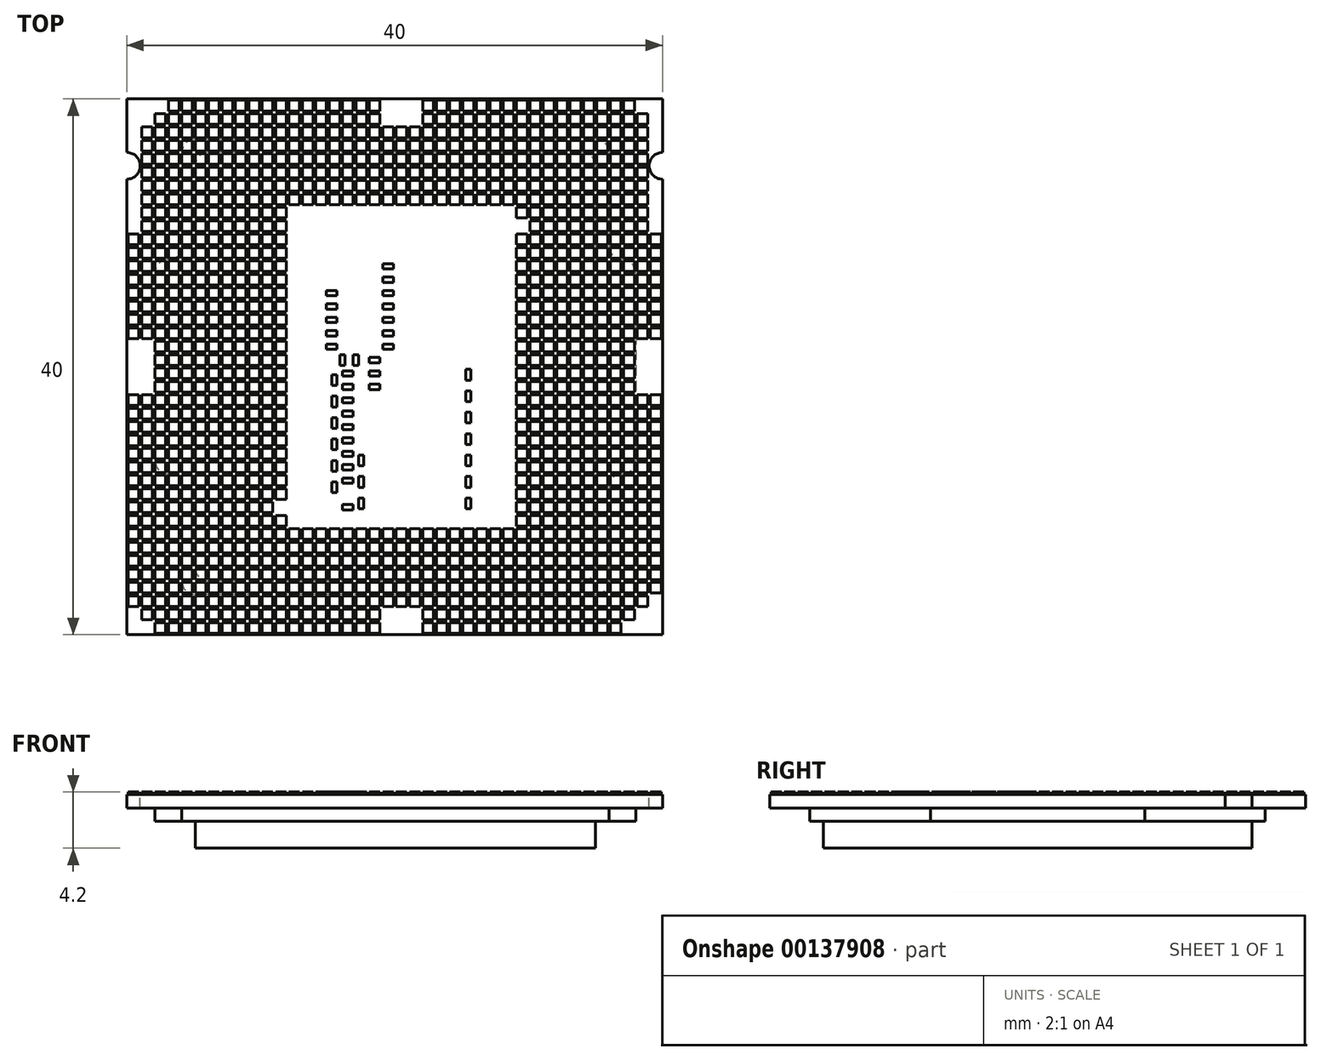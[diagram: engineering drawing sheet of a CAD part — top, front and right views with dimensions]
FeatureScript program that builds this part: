
annotation { "Feature Type Name" : "Feature", "Feature Type Description" : "" }
export const myFeature = defineFeature(function(context is Context, id is Id, definition is map)
    precondition{}
    {
        {
            var Q0;
            Q0=qCreatedBy(makeId("Top.planeOp"),FACE);
            var sketch = newSketch(context, id + "F0", { "sketchPlane" : qUnion([Q0])});
            skLineSegment(sketch, "E0.bottom", {"start": v(0, 0) * mm, "end": v(40, 0) * mm});
            skLineSegment(sketch, "E0.top", {"start": v(0, 40) * mm, "end": v(40, 40) * mm});
            skLineSegment(sketch, "E0.left", {"start": v(0, 0) * mm, "end": v(0, 40) * mm});
            skLineSegment(sketch, "E0.right", {"start": v(40, 0) * mm, "end": v(40, 40) * mm});
            skSolve(sketch);
        }
        {
            var Q0;
            Q0 = qSketchRegion(id + "F0", true);
            extrude(context, id + "F1", {"entities" : qUnion([Q0]), "oppositeDirection" : true, "depth" : 1 * mm});
        }
        {
            var Q0;
            Q0=makeQuery(id+"F1.opExtrude","CAP_FACE",FACE,{"disambiguationData":[OSD([sQuery(id+"F0.wireOp",EDGE,"E0.bottom"),sQuery(id+"F0.wireOp",EDGE,"E0.top"),sQuery(id+"F0.wireOp",EDGE,"E0.left"),sQuery(id+"F0.wireOp",EDGE,"E0.right")])],"isStart":true});
            var sketch = newSketch(context, id + "F2", { "sketchPlane" : qUnion([Q0])});
            skCircle(sketch, "E1", {"center": v(0, 35) * mm, "radius": 1 * mm});
            skCircle(sketch, "E2", {"center": v(40, 35) * mm, "radius": 1 * mm});
            skSolve(sketch);
        }
        {
            var Q0;
            Q0 = qSketchRegion(id + "F2", true);
            extrude(context, id + "F3", {"entities" : qUnion([Q0]), "operationType" : NewBodyOperationType.REMOVE, "oppositeDirection" : true, "depth" : 1 * mm});
        }
        {
            var Q0;
            Q0=makeQuery(id+"F1.opExtrude","CAP_FACE",FACE,{"disambiguationData":[OSD([sQuery(id+"F0.wireOp",EDGE,"E0.bottom"),sQuery(id+"F0.wireOp",EDGE,"E0.top"),sQuery(id+"F0.wireOp",EDGE,"E0.left"),sQuery(id+"F0.wireOp",EDGE,"E0.right")])],"isStart":true});
            var sketch = newSketch(context, id + "F4", { "sketchPlane" : qUnion([Q0])});
            skLineSegment(sketch, "E3.bottom", {"start": v(0.1, 30) * mm, "end": v(1, 30) * mm});
            skLineSegment(sketch, "E3.top", {"start": v(0.1, 22) * mm, "end": v(1, 22) * mm});
            skLineSegment(sketch, "E3.left", {"start": v(0.1, 30) * mm, "end": v(0.1, 22) * mm});
            skLineSegment(sketch, "E3.right", {"start": v(1, 30) * mm, "end": v(1, 22) * mm});
            skLineSegment(sketch, "E4.bottom", {"start": v(1, 2) * mm, "end": v(0.1, 2) * mm});
            skLineSegment(sketch, "E4.top", {"start": v(1, 18) * mm, "end": v(0.1, 18) * mm});
            skLineSegment(sketch, "E4.left", {"start": v(1, 2) * mm, "end": v(1, 18) * mm});
            skLineSegment(sketch, "E4.right", {"start": v(0.1, 2) * mm, "end": v(0.1, 18) * mm});
            skLineSegment(sketch, "E5.bottom", {"start": v(1, 22) * mm, "end": v(2, 22) * mm});
            skLineSegment(sketch, "E5.top", {"start": v(1, 38) * mm, "end": v(2, 38) * mm});
            skLineSegment(sketch, "E5.left", {"start": v(1, 22) * mm, "end": v(1, 38) * mm});
            skLineSegment(sketch, "E5.right", {"start": v(2, 22) * mm, "end": v(2, 38) * mm});
            skLineSegment(sketch, "E6.bottom", {"start": v(2, 39) * mm, "end": v(3, 39) * mm});
            skLineSegment(sketch, "E6.top", {"start": v(2, 0) * mm, "end": v(3, 0) * mm});
            skLineSegment(sketch, "E6.left", {"start": v(2, 39) * mm, "end": v(2, 0) * mm});
            skLineSegment(sketch, "E6.right", {"start": v(3, 39) * mm, "end": v(3, 0) * mm});
            skLineSegment(sketch, "E7.bottom", {"start": v(1, 18) * mm, "end": v(2, 18) * mm});
            skLineSegment(sketch, "E7.top", {"start": v(1, 1) * mm, "end": v(2, 1) * mm});
            skLineSegment(sketch, "E7.left", {"start": v(1, 18) * mm, "end": v(1, 1) * mm});
            skLineSegment(sketch, "E7.right", {"start": v(2, 18) * mm, "end": v(2, 1) * mm});
            skLineSegment(sketch, "E8.bottom", {"start": v(11, 40) * mm, "end": v(3, 40) * mm});
            skLineSegment(sketch, "E8.top", {"start": v(11, 0) * mm, "end": v(3, 0) * mm});
            skLineSegment(sketch, "E8.left", {"start": v(11, 40) * mm, "end": v(11, 0) * mm});
            skLineSegment(sketch, "E8.right", {"start": v(3, 40) * mm, "end": v(3, 0) * mm});
            skLineSegment(sketch, "E9.bottom", {"start": v(11, 40) * mm, "end": v(12, 40) * mm});
            skLineSegment(sketch, "E9.top", {"start": v(11, 10) * mm, "end": v(12, 10) * mm});
            skLineSegment(sketch, "E9.left", {"start": v(11, 40) * mm, "end": v(11, 10) * mm});
            skLineSegment(sketch, "E9.right", {"start": v(12, 40) * mm, "end": v(12, 10) * mm});
            skLineSegment(sketch, "E10.bottom", {"start": v(11, 0) * mm, "end": v(12, 0) * mm});
            skLineSegment(sketch, "E10.top", {"start": v(11, 9) * mm, "end": v(12, 9) * mm});
            skLineSegment(sketch, "E10.left", {"start": v(11, 0) * mm, "end": v(11, 9) * mm});
            skLineSegment(sketch, "E10.right", {"start": v(12, 0) * mm, "end": v(12, 9) * mm});
            skLineSegment(sketch, "E11.bottom", {"start": v(12, 40) * mm, "end": v(19, 40) * mm});
            skLineSegment(sketch, "E11.top", {"start": v(12, 32) * mm, "end": v(19, 32) * mm});
            skLineSegment(sketch, "E11.left", {"start": v(12, 40) * mm, "end": v(12, 32) * mm});
            skLineSegment(sketch, "E11.right", {"start": v(19, 40) * mm, "end": v(19, 32) * mm});
            skLineSegment(sketch, "E12.bottom", {"start": v(12, 0) * mm, "end": v(19, 0) * mm});
            skLineSegment(sketch, "E12.top", {"start": v(12, 8) * mm, "end": v(19, 8) * mm});
            skLineSegment(sketch, "E12.left", {"start": v(12, 0) * mm, "end": v(12, 8) * mm});
            skLineSegment(sketch, "E12.right", {"start": v(19, 0) * mm, "end": v(19, 8) * mm});
            skLineSegment(sketch, "E13.bottom", {"start": v(19, 8) * mm, "end": v(22, 8) * mm});
            skLineSegment(sketch, "E13.top", {"start": v(19, 2) * mm, "end": v(22, 2) * mm});
            skLineSegment(sketch, "E13.left", {"start": v(19, 8) * mm, "end": v(19, 2) * mm});
            skLineSegment(sketch, "E13.right", {"start": v(22, 8) * mm, "end": v(22, 2) * mm});
            skLineSegment(sketch, "E14.bottom", {"start": v(19, 32) * mm, "end": v(22, 32) * mm});
            skLineSegment(sketch, "E14.top", {"start": v(19, 38) * mm, "end": v(22, 38) * mm});
            skLineSegment(sketch, "E14.left", {"start": v(19, 32) * mm, "end": v(19, 38) * mm});
            skLineSegment(sketch, "E14.right", {"start": v(22, 32) * mm, "end": v(22, 38) * mm});
            skLineSegment(sketch, "E15.bottom", {"start": v(22, 32) * mm, "end": v(29, 32) * mm});
            skLineSegment(sketch, "E15.top", {"start": v(22, 40) * mm, "end": v(29, 40) * mm});
            skLineSegment(sketch, "E15.left", {"start": v(22, 32) * mm, "end": v(22, 40) * mm});
            skLineSegment(sketch, "E15.right", {"start": v(29, 32) * mm, "end": v(29, 40) * mm});
            skPoint(sketch, "E16.oppositeSnap0", {"position": v(0.1, 10) * mm});
            skLineSegment(sketch, "E17.bottom", {"start": v(22, 8) * mm, "end": v(29, 8) * mm});
            skLineSegment(sketch, "E17.top", {"start": v(22, 0) * mm, "end": v(29, 0) * mm});
            skLineSegment(sketch, "E17.left", {"start": v(22, 8) * mm, "end": v(22, 0) * mm});
            skLineSegment(sketch, "E17.right", {"start": v(29, 8) * mm, "end": v(29, 0) * mm});
            skLineSegment(sketch, "E18.bottom", {"start": v(29, 40) * mm, "end": v(30, 40) * mm});
            skLineSegment(sketch, "E18.top", {"start": v(29, 31) * mm, "end": v(30, 31) * mm});
            skLineSegment(sketch, "E18.left", {"start": v(29, 40) * mm, "end": v(29, 31) * mm});
            skLineSegment(sketch, "E18.right", {"start": v(30, 40) * mm, "end": v(30, 31) * mm});
            skLineSegment(sketch, "E19.bottom", {"start": v(29, 0) * mm, "end": v(30, 0) * mm});
            skLineSegment(sketch, "E19.top", {"start": v(29, 30) * mm, "end": v(30, 30) * mm});
            skLineSegment(sketch, "E19.left", {"start": v(29, 0) * mm, "end": v(29, 30) * mm});
            skLineSegment(sketch, "E19.right", {"start": v(30, 0) * mm, "end": v(30, 30) * mm});
            skLineSegment(sketch, "E20.bottom", {"start": v(30, 40) * mm, "end": v(37, 40) * mm});
            skLineSegment(sketch, "E20.top", {"start": v(30, 0) * mm, "end": v(37, 0) * mm});
            skLineSegment(sketch, "E20.left", {"start": v(30, 40) * mm, "end": v(30, 0) * mm});
            skLineSegment(sketch, "E20.right", {"start": v(37, 40) * mm, "end": v(37, 0) * mm});
            skLineSegment(sketch, "E21.bottom", {"start": v(37, 40) * mm, "end": v(38, 40) * mm});
            skLineSegment(sketch, "E21.top", {"start": v(37, 1) * mm, "end": v(38, 1) * mm});
            skLineSegment(sketch, "E21.left", {"start": v(37, 40) * mm, "end": v(37, 1) * mm});
            skLineSegment(sketch, "E21.right", {"start": v(38, 40) * mm, "end": v(38, 1) * mm});
            skLineSegment(sketch, "E22.bottom", {"start": v(38, 39) * mm, "end": v(39, 39) * mm});
            skLineSegment(sketch, "E22.top", {"start": v(38, 22) * mm, "end": v(39, 22) * mm});
            skLineSegment(sketch, "E22.left", {"start": v(38, 39) * mm, "end": v(38, 22) * mm});
            skLineSegment(sketch, "E22.right", {"start": v(39, 39) * mm, "end": v(39, 22) * mm});
            skLineSegment(sketch, "E23.bottom", {"start": v(38, 18) * mm, "end": v(39, 18) * mm});
            skLineSegment(sketch, "E23.top", {"start": v(38, 2) * mm, "end": v(39, 2) * mm});
            skLineSegment(sketch, "E23.left", {"start": v(38, 18) * mm, "end": v(38, 2) * mm});
            skLineSegment(sketch, "E23.right", {"start": v(39, 18) * mm, "end": v(39, 2) * mm});
            skLineSegment(sketch, "E24.bottom", {"start": v(39, 18) * mm, "end": v(39.9, 18) * mm});
            skLineSegment(sketch, "E24.top", {"start": v(39, 3) * mm, "end": v(39.9, 3) * mm});
            skLineSegment(sketch, "E24.left", {"start": v(39, 18) * mm, "end": v(39, 3) * mm});
            skLineSegment(sketch, "E24.right", {"start": v(39.9, 18) * mm, "end": v(39.9, 3) * mm});
            skLineSegment(sketch, "E25.bottom", {"start": v(39, 22) * mm, "end": v(39.9, 22) * mm});
            skLineSegment(sketch, "E25.top", {"start": v(39, 30) * mm, "end": v(39.9, 30) * mm});
            skLineSegment(sketch, "E25.left", {"start": v(39, 22) * mm, "end": v(39, 30) * mm});
            skLineSegment(sketch, "E25.right", {"start": v(39.9, 22) * mm, "end": v(39.9, 30) * mm});
            skSolve(sketch);
        }
        {
            var Q0;
            Q0 = qSketchRegion(id + "F4", true);
            extrude(context, id + "F5", {"entities" : qUnion([Q0]), "depth" : 0.2 * mm});
        }
        {
            var Q0;
            Q0=makeQuery(id+"F1.opExtrude","CAP_FACE",FACE,{"disambiguationData":[OSD([sQuery(id+"F0.wireOp",EDGE,"E0.bottom"),sQuery(id+"F0.wireOp",EDGE,"E0.top"),sQuery(id+"F0.wireOp",EDGE,"E0.left"),sQuery(id+"F0.wireOp",EDGE,"E0.right")])],"isStart":true});
            var sketch = newSketch(context, id + "F6", { "sketchPlane" : qUnion([Q0])});
            skLineSegment(sketch, "E26.bottom", {"start": v(0.9, 40) * mm, "end": v(1.1, 40) * mm});
            skLineSegment(sketch, "E26.top", {"start": v(0.9, 0) * mm, "end": v(1.1, 0) * mm});
            skLineSegment(sketch, "E26.left", {"start": v(0.9, 40) * mm, "end": v(0.9, 0) * mm});
            skLineSegment(sketch, "E26.right", {"start": v(1.1, 40) * mm, "end": v(1.1, 0) * mm});
            skLineSegment(sketch, "E27.bottom", {"start": v(1.9, 40) * mm, "end": v(2.1, 40) * mm});
            skLineSegment(sketch, "E27.top", {"start": v(1.9, 0) * mm, "end": v(2.1, 0) * mm});
            skLineSegment(sketch, "E27.left", {"start": v(1.9, 40) * mm, "end": v(1.9, 0) * mm});
            skLineSegment(sketch, "E27.right", {"start": v(2.1, 40) * mm, "end": v(2.1, 0) * mm});
            skLineSegment(sketch, "E28.bottom", {"start": v(2.9, 40) * mm, "end": v(3.1, 40) * mm});
            skLineSegment(sketch, "E28.top", {"start": v(2.9, 0) * mm, "end": v(3.1, 0) * mm});
            skLineSegment(sketch, "E28.left", {"start": v(2.9, 40) * mm, "end": v(2.9, 0) * mm});
            skLineSegment(sketch, "E28.right", {"start": v(3.1, 40) * mm, "end": v(3.1, 0) * mm});
            skLineSegment(sketch, "E29.bottom", {"start": v(3.9, 40) * mm, "end": v(4.1, 40) * mm});
            skLineSegment(sketch, "E29.top", {"start": v(3.9, 0) * mm, "end": v(4.1, 0) * mm});
            skLineSegment(sketch, "E29.left", {"start": v(3.9, 40) * mm, "end": v(3.9, 0) * mm});
            skLineSegment(sketch, "E29.right", {"start": v(4.1, 40) * mm, "end": v(4.1, 0) * mm});
            skLineSegment(sketch, "E30.bottom", {"start": v(4.9, 40) * mm, "end": v(5.1, 40) * mm});
            skLineSegment(sketch, "E30.top", {"start": v(4.9, 0) * mm, "end": v(5.1, 0) * mm});
            skLineSegment(sketch, "E30.left", {"start": v(4.9, 40) * mm, "end": v(4.9, 0) * mm});
            skLineSegment(sketch, "E30.right", {"start": v(5.1, 40) * mm, "end": v(5.1, 0) * mm});
            skLineSegment(sketch, "E31.bottom", {"start": v(5.9, 40) * mm, "end": v(6.1, 40) * mm});
            skLineSegment(sketch, "E31.top", {"start": v(5.9, 0) * mm, "end": v(6.1, 0) * mm});
            skLineSegment(sketch, "E31.left", {"start": v(5.9, 40) * mm, "end": v(5.9, 0) * mm});
            skLineSegment(sketch, "E31.right", {"start": v(6.1, 40) * mm, "end": v(6.1, 0) * mm});
            skLineSegment(sketch, "E32.bottom", {"start": v(6.9, 40) * mm, "end": v(7.1, 40) * mm});
            skLineSegment(sketch, "E32.top", {"start": v(6.9, 0) * mm, "end": v(7.1, 0) * mm});
            skLineSegment(sketch, "E32.left", {"start": v(6.9, 40) * mm, "end": v(6.9, 0) * mm});
            skLineSegment(sketch, "E32.right", {"start": v(7.1, 40) * mm, "end": v(7.1, 0) * mm});
            skLineSegment(sketch, "E33.bottom", {"start": v(7.9, 40) * mm, "end": v(8.1, 40) * mm});
            skLineSegment(sketch, "E33.top", {"start": v(7.9, 0) * mm, "end": v(8.1, 0) * mm});
            skLineSegment(sketch, "E33.left", {"start": v(7.9, 40) * mm, "end": v(7.9, 0) * mm});
            skLineSegment(sketch, "E33.right", {"start": v(8.1, 40) * mm, "end": v(8.1, 0) * mm});
            skLineSegment(sketch, "E34.bottom", {"start": v(8.9, 40) * mm, "end": v(9.1, 40) * mm});
            skLineSegment(sketch, "E34.top", {"start": v(8.9, 0) * mm, "end": v(9.1, 0) * mm});
            skLineSegment(sketch, "E34.left", {"start": v(8.9, 40) * mm, "end": v(8.9, 0) * mm});
            skLineSegment(sketch, "E34.right", {"start": v(9.1, 40) * mm, "end": v(9.1, 0) * mm});
            skLineSegment(sketch, "E35.bottom", {"start": v(9.9, 40) * mm, "end": v(10.1, 40) * mm});
            skLineSegment(sketch, "E35.top", {"start": v(9.9, 0) * mm, "end": v(10.1, 0) * mm});
            skLineSegment(sketch, "E35.left", {"start": v(9.9, 40) * mm, "end": v(9.9, 0) * mm});
            skLineSegment(sketch, "E35.right", {"start": v(10.1, 40) * mm, "end": v(10.1, 0) * mm});
            skLineSegment(sketch, "E36.bottom", {"start": v(10.9, 40) * mm, "end": v(11.1, 40) * mm});
            skLineSegment(sketch, "E36.top", {"start": v(10.9, 0) * mm, "end": v(11.1, 0) * mm});
            skLineSegment(sketch, "E36.left", {"start": v(10.9, 40) * mm, "end": v(10.9, 0) * mm});
            skLineSegment(sketch, "E36.right", {"start": v(11.1, 40) * mm, "end": v(11.1, 0) * mm});
            skLineSegment(sketch, "E37.bottom", {"start": v(11.9, 40) * mm, "end": v(12.1, 40) * mm});
            skLineSegment(sketch, "E37.top", {"start": v(11.9, 0) * mm, "end": v(12.1, 0) * mm});
            skLineSegment(sketch, "E37.left", {"start": v(11.9, 40) * mm, "end": v(11.9, 0) * mm});
            skLineSegment(sketch, "E37.right", {"start": v(12.1, 40) * mm, "end": v(12.1, 0) * mm});
            skLineSegment(sketch, "E38.bottom", {"start": v(12.9, 40) * mm, "end": v(13.1, 40) * mm});
            skLineSegment(sketch, "E38.top", {"start": v(12.9, 0) * mm, "end": v(13.1, 0) * mm});
            skLineSegment(sketch, "E38.left", {"start": v(12.9, 40) * mm, "end": v(12.9, 0) * mm});
            skLineSegment(sketch, "E38.right", {"start": v(13.1, 40) * mm, "end": v(13.1, 0) * mm});
            skLineSegment(sketch, "E39.bottom", {"start": v(13.9, 40) * mm, "end": v(14.1, 40) * mm});
            skLineSegment(sketch, "E39.top", {"start": v(13.9, 0) * mm, "end": v(14.1, 0) * mm});
            skLineSegment(sketch, "E39.left", {"start": v(13.9, 40) * mm, "end": v(13.9, 0) * mm});
            skLineSegment(sketch, "E39.right", {"start": v(14.1, 40) * mm, "end": v(14.1, 0) * mm});
            skLineSegment(sketch, "E40.bottom", {"start": v(14.9, 40) * mm, "end": v(15.1, 40) * mm});
            skLineSegment(sketch, "E40.top", {"start": v(14.9, 0) * mm, "end": v(15.1, 0) * mm});
            skLineSegment(sketch, "E40.left", {"start": v(14.9, 40) * mm, "end": v(14.9, 0) * mm});
            skLineSegment(sketch, "E40.right", {"start": v(15.1, 40) * mm, "end": v(15.1, 0) * mm});
            skLineSegment(sketch, "E41.bottom", {"start": v(15.9, 40) * mm, "end": v(16.1, 40) * mm});
            skLineSegment(sketch, "E41.top", {"start": v(15.9, 0) * mm, "end": v(16.1, 0) * mm});
            skLineSegment(sketch, "E41.left", {"start": v(15.9, 40) * mm, "end": v(15.9, 0) * mm});
            skLineSegment(sketch, "E41.right", {"start": v(16.1, 40) * mm, "end": v(16.1, 0) * mm});
            skLineSegment(sketch, "E42.bottom", {"start": v(16.9, 40) * mm, "end": v(17.1, 40) * mm});
            skLineSegment(sketch, "E42.top", {"start": v(16.9, 0) * mm, "end": v(17.1, 0) * mm});
            skLineSegment(sketch, "E42.left", {"start": v(16.9, 40) * mm, "end": v(16.9, 0) * mm});
            skLineSegment(sketch, "E42.right", {"start": v(17.1, 40) * mm, "end": v(17.1, 0) * mm});
            skLineSegment(sketch, "E43.bottom", {"start": v(17.9, 40) * mm, "end": v(18.1, 40) * mm});
            skLineSegment(sketch, "E43.top", {"start": v(17.9, 0) * mm, "end": v(18.1, 0) * mm});
            skLineSegment(sketch, "E43.left", {"start": v(17.9, 40) * mm, "end": v(17.9, 0) * mm});
            skLineSegment(sketch, "E43.right", {"start": v(18.1, 40) * mm, "end": v(18.1, 0) * mm});
            skLineSegment(sketch, "E44.bottom", {"start": v(18.9, 40) * mm, "end": v(19.1, 40) * mm});
            skLineSegment(sketch, "E44.top", {"start": v(18.9, 0) * mm, "end": v(19.1, 0) * mm});
            skLineSegment(sketch, "E44.left", {"start": v(18.9, 40) * mm, "end": v(18.9, 0) * mm});
            skLineSegment(sketch, "E44.right", {"start": v(19.1, 40) * mm, "end": v(19.1, 0) * mm});
            skLineSegment(sketch, "E45.bottom", {"start": v(19.9, 40) * mm, "end": v(20.1, 40) * mm});
            skLineSegment(sketch, "E45.top", {"start": v(19.9, 0) * mm, "end": v(20.1, 0) * mm});
            skLineSegment(sketch, "E45.left", {"start": v(19.9, 40) * mm, "end": v(19.9, 0) * mm});
            skLineSegment(sketch, "E45.right", {"start": v(20.1, 40) * mm, "end": v(20.1, 0) * mm});
            skLineSegment(sketch, "E46.bottom", {"start": v(20.9, 40) * mm, "end": v(21.1, 40) * mm});
            skLineSegment(sketch, "E46.top", {"start": v(20.9, 0) * mm, "end": v(21.1, 0) * mm});
            skLineSegment(sketch, "E46.left", {"start": v(20.9, 40) * mm, "end": v(20.9, 0) * mm});
            skLineSegment(sketch, "E46.right", {"start": v(21.1, 40) * mm, "end": v(21.1, 0) * mm});
            skLineSegment(sketch, "E47.bottom", {"start": v(21.9, 40) * mm, "end": v(22.1, 40) * mm});
            skLineSegment(sketch, "E47.top", {"start": v(21.9, 0) * mm, "end": v(22.1, 0) * mm});
            skLineSegment(sketch, "E47.left", {"start": v(21.9, 40) * mm, "end": v(21.9, 0) * mm});
            skLineSegment(sketch, "E47.right", {"start": v(22.1, 40) * mm, "end": v(22.1, 0) * mm});
            skLineSegment(sketch, "E48.bottom", {"start": v(22.9, 40) * mm, "end": v(23.1, 40) * mm});
            skLineSegment(sketch, "E48.top", {"start": v(22.9, 0) * mm, "end": v(23.1, 0) * mm});
            skLineSegment(sketch, "E48.left", {"start": v(22.9, 40) * mm, "end": v(22.9, 0) * mm});
            skLineSegment(sketch, "E48.right", {"start": v(23.1, 40) * mm, "end": v(23.1, 0) * mm});
            skLineSegment(sketch, "E49.bottom", {"start": v(23.9, 40) * mm, "end": v(24.1, 40) * mm});
            skLineSegment(sketch, "E49.top", {"start": v(23.9, 0) * mm, "end": v(24.1, 0) * mm});
            skLineSegment(sketch, "E49.left", {"start": v(23.9, 40) * mm, "end": v(23.9, 0) * mm});
            skLineSegment(sketch, "E49.right", {"start": v(24.1, 40) * mm, "end": v(24.1, 0) * mm});
            skLineSegment(sketch, "E50.bottom", {"start": v(24.9, 40) * mm, "end": v(25.1, 40) * mm});
            skLineSegment(sketch, "E50.top", {"start": v(24.9, 0) * mm, "end": v(25.1, 0) * mm});
            skLineSegment(sketch, "E50.left", {"start": v(24.9, 40) * mm, "end": v(24.9, 0) * mm});
            skLineSegment(sketch, "E50.right", {"start": v(25.1, 40) * mm, "end": v(25.1, 0) * mm});
            skLineSegment(sketch, "E51.bottom", {"start": v(25.9, 40) * mm, "end": v(26.1, 40) * mm});
            skLineSegment(sketch, "E51.top", {"start": v(25.9, 0) * mm, "end": v(26.1, 0) * mm});
            skLineSegment(sketch, "E51.left", {"start": v(25.9, 40) * mm, "end": v(25.9, 0) * mm});
            skLineSegment(sketch, "E51.right", {"start": v(26.1, 40) * mm, "end": v(26.1, 0) * mm});
            skLineSegment(sketch, "E52.bottom", {"start": v(26.9, 40) * mm, "end": v(27.1, 40) * mm});
            skLineSegment(sketch, "E52.top", {"start": v(26.9, 0) * mm, "end": v(27.1, 0) * mm});
            skLineSegment(sketch, "E52.left", {"start": v(26.9, 40) * mm, "end": v(26.9, 0) * mm});
            skLineSegment(sketch, "E52.right", {"start": v(27.1, 40) * mm, "end": v(27.1, 0) * mm});
            skLineSegment(sketch, "E53.bottom", {"start": v(27.9, 40) * mm, "end": v(28.1, 40) * mm});
            skLineSegment(sketch, "E53.top", {"start": v(27.9, 0) * mm, "end": v(28.1, 0) * mm});
            skLineSegment(sketch, "E53.left", {"start": v(27.9, 40) * mm, "end": v(27.9, 0) * mm});
            skLineSegment(sketch, "E53.right", {"start": v(28.1, 40) * mm, "end": v(28.1, 0) * mm});
            skLineSegment(sketch, "E54.bottom", {"start": v(28.9, 40) * mm, "end": v(29.1, 40) * mm});
            skLineSegment(sketch, "E54.top", {"start": v(28.9, 0) * mm, "end": v(29.1, 0) * mm});
            skLineSegment(sketch, "E54.left", {"start": v(28.9, 40) * mm, "end": v(28.9, 0) * mm});
            skLineSegment(sketch, "E54.right", {"start": v(29.1, 40) * mm, "end": v(29.1, 0) * mm});
            skLineSegment(sketch, "E55.bottom", {"start": v(29.9, 40) * mm, "end": v(30.1, 40) * mm});
            skLineSegment(sketch, "E55.top", {"start": v(29.9, 0) * mm, "end": v(30.1, 0) * mm});
            skLineSegment(sketch, "E55.left", {"start": v(29.9, 40) * mm, "end": v(29.9, 0) * mm});
            skLineSegment(sketch, "E55.right", {"start": v(30.1, 40) * mm, "end": v(30.1, 0) * mm});
            skLineSegment(sketch, "E56.bottom", {"start": v(30.9, 40) * mm, "end": v(31.1, 40) * mm});
            skLineSegment(sketch, "E56.top", {"start": v(30.9, 0) * mm, "end": v(31.1, 0) * mm});
            skLineSegment(sketch, "E56.left", {"start": v(30.9, 40) * mm, "end": v(30.9, 0) * mm});
            skLineSegment(sketch, "E56.right", {"start": v(31.1, 40) * mm, "end": v(31.1, 0) * mm});
            skLineSegment(sketch, "E57.bottom", {"start": v(31.9, 40) * mm, "end": v(32.1, 40) * mm});
            skLineSegment(sketch, "E57.top", {"start": v(31.9, 0) * mm, "end": v(32.1, 0) * mm});
            skLineSegment(sketch, "E57.left", {"start": v(31.9, 40) * mm, "end": v(31.9, 0) * mm});
            skLineSegment(sketch, "E57.right", {"start": v(32.1, 40) * mm, "end": v(32.1, 0) * mm});
            skLineSegment(sketch, "E58.bottom", {"start": v(32.9, 40) * mm, "end": v(33.1, 40) * mm});
            skLineSegment(sketch, "E58.top", {"start": v(32.9, 0) * mm, "end": v(33.1, 0) * mm});
            skLineSegment(sketch, "E58.left", {"start": v(32.9, 40) * mm, "end": v(32.9, 0) * mm});
            skLineSegment(sketch, "E58.right", {"start": v(33.1, 40) * mm, "end": v(33.1, 0) * mm});
            skLineSegment(sketch, "E59.bottom", {"start": v(33.9, 40) * mm, "end": v(34.1, 40) * mm});
            skLineSegment(sketch, "E59.top", {"start": v(33.9, 0) * mm, "end": v(34.1, 0) * mm});
            skLineSegment(sketch, "E59.left", {"start": v(33.9, 40) * mm, "end": v(33.9, 0) * mm});
            skLineSegment(sketch, "E59.right", {"start": v(34.1, 40) * mm, "end": v(34.1, 0) * mm});
            skLineSegment(sketch, "E60.bottom", {"start": v(34.9, 40) * mm, "end": v(35.1, 40) * mm});
            skLineSegment(sketch, "E60.top", {"start": v(34.9, 0) * mm, "end": v(35.1, 0) * mm});
            skLineSegment(sketch, "E60.left", {"start": v(34.9, 40) * mm, "end": v(34.9, 0) * mm});
            skLineSegment(sketch, "E60.right", {"start": v(35.1, 40) * mm, "end": v(35.1, 0) * mm});
            skLineSegment(sketch, "E61.bottom", {"start": v(35.9, 40) * mm, "end": v(36.1, 40) * mm});
            skLineSegment(sketch, "E61.top", {"start": v(35.9, 0) * mm, "end": v(36.1, 0) * mm});
            skLineSegment(sketch, "E61.left", {"start": v(35.9, 40) * mm, "end": v(35.9, 0) * mm});
            skLineSegment(sketch, "E61.right", {"start": v(36.1, 40) * mm, "end": v(36.1, 0) * mm});
            skLineSegment(sketch, "E62.bottom", {"start": v(36.9, 40) * mm, "end": v(37.1, 40) * mm});
            skLineSegment(sketch, "E62.top", {"start": v(36.9, 0) * mm, "end": v(37.1, 0) * mm});
            skLineSegment(sketch, "E62.left", {"start": v(36.9, 40) * mm, "end": v(36.9, 0) * mm});
            skLineSegment(sketch, "E62.right", {"start": v(37.1, 40) * mm, "end": v(37.1, 0) * mm});
            skLineSegment(sketch, "E63.bottom", {"start": v(37.9, 40) * mm, "end": v(38.1, 40) * mm});
            skLineSegment(sketch, "E63.top", {"start": v(37.9, 0) * mm, "end": v(38.1, 0) * mm});
            skLineSegment(sketch, "E63.left", {"start": v(37.9, 40) * mm, "end": v(37.9, 0) * mm});
            skLineSegment(sketch, "E63.right", {"start": v(38.1, 40) * mm, "end": v(38.1, 0) * mm});
            skLineSegment(sketch, "E64.bottom", {"start": v(38.9, 40) * mm, "end": v(39.1, 40) * mm});
            skLineSegment(sketch, "E64.top", {"start": v(38.9, 0) * mm, "end": v(39.1, 0) * mm});
            skLineSegment(sketch, "E64.left", {"start": v(38.9, 40) * mm, "end": v(38.9, 0) * mm});
            skLineSegment(sketch, "E64.right", {"start": v(39.1, 40) * mm, "end": v(39.1, 0) * mm});
            skSolve(sketch);
        }
        {
            var Q0;
            Q0=makeQuery(id+"F1.opExtrude","CAP_FACE",FACE,{"disambiguationData":[OSD([sQuery(id+"F0.wireOp",EDGE,"E0.bottom"),sQuery(id+"F0.wireOp",EDGE,"E0.top"),sQuery(id+"F0.wireOp",EDGE,"E0.left"),sQuery(id+"F0.wireOp",EDGE,"E0.right")])],"isStart":true});
            var sketch = newSketch(context, id + "F7", { "sketchPlane" : qUnion([Q0])});
            skLineSegment(sketch, "E65.bottom", {"start": v(40, 40) * mm, "end": v(0, 40) * mm});
            skLineSegment(sketch, "E65.top", {"start": v(40, 39.9) * mm, "end": v(0, 39.9) * mm});
            skLineSegment(sketch, "E65.left", {"start": v(40, 40) * mm, "end": v(40, 39.9) * mm});
            skLineSegment(sketch, "E65.right", {"start": v(0, 40) * mm, "end": v(0, 39.9) * mm});
            skLineSegment(sketch, "E66.bottom", {"start": v(40, 0) * mm, "end": v(0, 0) * mm});
            skLineSegment(sketch, "E66.top", {"start": v(40, 0.1) * mm, "end": v(0, 0.1) * mm});
            skLineSegment(sketch, "E66.left", {"start": v(40, 0) * mm, "end": v(40, 0.1) * mm});
            skLineSegment(sketch, "E66.right", {"start": v(0, 0) * mm, "end": v(0, 0.1) * mm});
            skLineSegment(sketch, "E67.bottom", {"start": v(40, 39.1) * mm, "end": v(0, 39.1) * mm});
            skLineSegment(sketch, "E67.top", {"start": v(40, 38.9) * mm, "end": v(0, 38.9) * mm});
            skLineSegment(sketch, "E67.left", {"start": v(40, 39.1) * mm, "end": v(40, 38.9) * mm});
            skLineSegment(sketch, "E67.right", {"start": v(0, 39.1) * mm, "end": v(0, 38.9) * mm});
            skLineSegment(sketch, "E68.bottom", {"start": v(40, 38.1) * mm, "end": v(0, 38.1) * mm});
            skLineSegment(sketch, "E68.top", {"start": v(40, 37.9) * mm, "end": v(0, 37.9) * mm});
            skLineSegment(sketch, "E68.left", {"start": v(40, 38.1) * mm, "end": v(40, 37.9) * mm});
            skLineSegment(sketch, "E68.right", {"start": v(0, 38.1) * mm, "end": v(0, 37.9) * mm});
            skLineSegment(sketch, "E69.bottom", {"start": v(40, 37.1) * mm, "end": v(0, 37.1) * mm});
            skLineSegment(sketch, "E69.top", {"start": v(40, 36.9) * mm, "end": v(0, 36.9) * mm});
            skLineSegment(sketch, "E69.left", {"start": v(40, 37.1) * mm, "end": v(40, 36.9) * mm});
            skLineSegment(sketch, "E69.right", {"start": v(0, 37.1) * mm, "end": v(0, 36.9) * mm});
            skLineSegment(sketch, "E70.bottom", {"start": v(40, 36.1) * mm, "end": v(0, 36.1) * mm});
            skLineSegment(sketch, "E70.top", {"start": v(40, 35.9) * mm, "end": v(0, 35.9) * mm});
            skLineSegment(sketch, "E70.left", {"start": v(40, 36.1) * mm, "end": v(40, 35.9) * mm});
            skLineSegment(sketch, "E70.right", {"start": v(0, 36.1) * mm, "end": v(0, 35.9) * mm});
            skLineSegment(sketch, "E71.bottom", {"start": v(40, 34.9) * mm, "end": v(0, 34.9) * mm});
            skLineSegment(sketch, "E71.top", {"start": v(40, 35.1) * mm, "end": v(0, 35.1) * mm});
            skLineSegment(sketch, "E71.left", {"start": v(40, 34.9) * mm, "end": v(40, 35.1) * mm});
            skLineSegment(sketch, "E71.right", {"start": v(0, 34.9) * mm, "end": v(0, 35.1) * mm});
            skLineSegment(sketch, "E72.bottom", {"start": v(40, 33.9) * mm, "end": v(0, 33.9) * mm});
            skLineSegment(sketch, "E72.top", {"start": v(40, 34.1) * mm, "end": v(0, 34.1) * mm});
            skLineSegment(sketch, "E72.left", {"start": v(40, 33.9) * mm, "end": v(40, 34.1) * mm});
            skLineSegment(sketch, "E72.right", {"start": v(0, 33.9) * mm, "end": v(0, 34.1) * mm});
            skLineSegment(sketch, "E73.bottom", {"start": v(40, 33.1) * mm, "end": v(0, 33.1) * mm});
            skLineSegment(sketch, "E73.top", {"start": v(40, 32.9) * mm, "end": v(0, 32.9) * mm});
            skLineSegment(sketch, "E73.left", {"start": v(40, 33.1) * mm, "end": v(40, 32.9) * mm});
            skLineSegment(sketch, "E73.right", {"start": v(0, 33.1) * mm, "end": v(0, 32.9) * mm});
            skLineSegment(sketch, "E74.bottom", {"start": v(40, 32.1) * mm, "end": v(0, 32.1) * mm});
            skLineSegment(sketch, "E74.top", {"start": v(40, 31.9) * mm, "end": v(0, 31.9) * mm});
            skLineSegment(sketch, "E74.left", {"start": v(40, 32.1) * mm, "end": v(40, 31.9) * mm});
            skLineSegment(sketch, "E74.right", {"start": v(0, 32.1) * mm, "end": v(0, 31.9) * mm});
            skLineSegment(sketch, "E75.bottom", {"start": v(40, 31.1) * mm, "end": v(0, 31.1) * mm});
            skLineSegment(sketch, "E75.top", {"start": v(40, 30.9) * mm, "end": v(0, 30.9) * mm});
            skLineSegment(sketch, "E75.left", {"start": v(40, 31.1) * mm, "end": v(40, 30.9) * mm});
            skLineSegment(sketch, "E75.right", {"start": v(0, 31.1) * mm, "end": v(0, 30.9) * mm});
            skLineSegment(sketch, "E76.bottom", {"start": v(40, 30.1) * mm, "end": v(0, 30.1) * mm});
            skLineSegment(sketch, "E76.top", {"start": v(40, 29.9) * mm, "end": v(0, 29.9) * mm});
            skLineSegment(sketch, "E76.left", {"start": v(40, 30.1) * mm, "end": v(40, 29.9) * mm});
            skLineSegment(sketch, "E76.right", {"start": v(0, 30.1) * mm, "end": v(0, 29.9) * mm});
            skLineSegment(sketch, "E77.bottom", {"start": v(40, 29.1) * mm, "end": v(0, 29.1) * mm});
            skLineSegment(sketch, "E77.top", {"start": v(40, 28.9) * mm, "end": v(0, 28.9) * mm});
            skLineSegment(sketch, "E77.left", {"start": v(40, 29.1) * mm, "end": v(40, 28.9) * mm});
            skLineSegment(sketch, "E77.right", {"start": v(0, 29.1) * mm, "end": v(0, 28.9) * mm});
            skLineSegment(sketch, "E78.bottom", {"start": v(40, 28.1) * mm, "end": v(0, 28.1) * mm});
            skLineSegment(sketch, "E78.top", {"start": v(40, 27.9) * mm, "end": v(0, 27.9) * mm});
            skLineSegment(sketch, "E78.left", {"start": v(40, 28.1) * mm, "end": v(40, 27.9) * mm});
            skLineSegment(sketch, "E78.right", {"start": v(0, 28.1) * mm, "end": v(0, 27.9) * mm});
            skLineSegment(sketch, "E79.bottom", {"start": v(40, 27.1) * mm, "end": v(0, 27.1) * mm});
            skLineSegment(sketch, "E79.top", {"start": v(40, 26.9) * mm, "end": v(0, 26.9) * mm});
            skLineSegment(sketch, "E79.left", {"start": v(40, 27.1) * mm, "end": v(40, 26.9) * mm});
            skLineSegment(sketch, "E79.right", {"start": v(0, 27.1) * mm, "end": v(0, 26.9) * mm});
            skLineSegment(sketch, "E80.bottom", {"start": v(40, 26.1) * mm, "end": v(0, 26.1) * mm});
            skLineSegment(sketch, "E80.top", {"start": v(40, 25.9) * mm, "end": v(0, 25.9) * mm});
            skLineSegment(sketch, "E80.left", {"start": v(40, 26.1) * mm, "end": v(40, 25.9) * mm});
            skLineSegment(sketch, "E80.right", {"start": v(0, 26.1) * mm, "end": v(0, 25.9) * mm});
            skLineSegment(sketch, "E81.bottom", {"start": v(40, 25.1) * mm, "end": v(0, 25.1) * mm});
            skLineSegment(sketch, "E81.top", {"start": v(40, 24.9) * mm, "end": v(0, 24.9) * mm});
            skLineSegment(sketch, "E81.left", {"start": v(40, 25.1) * mm, "end": v(40, 24.9) * mm});
            skLineSegment(sketch, "E81.right", {"start": v(0, 25.1) * mm, "end": v(0, 24.9) * mm});
            skLineSegment(sketch, "E82.bottom", {"start": v(40, 24.1) * mm, "end": v(0, 24.1) * mm});
            skLineSegment(sketch, "E82.top", {"start": v(40, 23.9) * mm, "end": v(0, 23.9) * mm});
            skLineSegment(sketch, "E82.left", {"start": v(40, 24.1) * mm, "end": v(40, 23.9) * mm});
            skLineSegment(sketch, "E82.right", {"start": v(0, 24.1) * mm, "end": v(0, 23.9) * mm});
            skLineSegment(sketch, "E83.bottom", {"start": v(40, 23.1) * mm, "end": v(0, 23.1) * mm});
            skLineSegment(sketch, "E83.top", {"start": v(40, 22.9) * mm, "end": v(0, 22.9) * mm});
            skLineSegment(sketch, "E83.left", {"start": v(40, 23.1) * mm, "end": v(40, 22.9) * mm});
            skLineSegment(sketch, "E83.right", {"start": v(0, 23.1) * mm, "end": v(0, 22.9) * mm});
            skLineSegment(sketch, "E84.bottom", {"start": v(40, 22.1) * mm, "end": v(0, 22.1) * mm});
            skLineSegment(sketch, "E84.top", {"start": v(40, 21.9) * mm, "end": v(0, 21.9) * mm});
            skLineSegment(sketch, "E84.left", {"start": v(40, 22.1) * mm, "end": v(40, 21.9) * mm});
            skLineSegment(sketch, "E84.right", {"start": v(0, 22.1) * mm, "end": v(0, 21.9) * mm});
            skLineSegment(sketch, "E85.bottom", {"start": v(40, 20.9) * mm, "end": v(0, 20.9) * mm});
            skLineSegment(sketch, "E85.top", {"start": v(40, 21.1) * mm, "end": v(0, 21.1) * mm});
            skLineSegment(sketch, "E85.left", {"start": v(40, 20.9) * mm, "end": v(40, 21.1) * mm});
            skLineSegment(sketch, "E85.right", {"start": v(0, 20.9) * mm, "end": v(0, 21.1) * mm});
            skLineSegment(sketch, "E86.bottom", {"start": v(40, 20.1) * mm, "end": v(0, 20.1) * mm});
            skLineSegment(sketch, "E86.top", {"start": v(40, 19.9) * mm, "end": v(0, 19.9) * mm});
            skLineSegment(sketch, "E86.left", {"start": v(40, 20.1) * mm, "end": v(40, 19.9) * mm});
            skLineSegment(sketch, "E86.right", {"start": v(0, 20.1) * mm, "end": v(0, 19.9) * mm});
            skLineSegment(sketch, "E87.bottom", {"start": v(40, 19.1) * mm, "end": v(0, 19.1) * mm});
            skLineSegment(sketch, "E87.top", {"start": v(40, 18.9) * mm, "end": v(0, 18.9) * mm});
            skLineSegment(sketch, "E87.left", {"start": v(40, 19.1) * mm, "end": v(40, 18.9) * mm});
            skLineSegment(sketch, "E87.right", {"start": v(0, 19.1) * mm, "end": v(0, 18.9) * mm});
            skLineSegment(sketch, "E88.bottom", {"start": v(40, 18.1) * mm, "end": v(0, 18.1) * mm});
            skLineSegment(sketch, "E88.top", {"start": v(40, 17.9) * mm, "end": v(0, 17.9) * mm});
            skLineSegment(sketch, "E88.left", {"start": v(40, 18.1) * mm, "end": v(40, 17.9) * mm});
            skLineSegment(sketch, "E88.right", {"start": v(0, 18.1) * mm, "end": v(0, 17.9) * mm});
            skLineSegment(sketch, "E89.bottom", {"start": v(40, 17.1) * mm, "end": v(0, 17.1) * mm});
            skLineSegment(sketch, "E89.top", {"start": v(40, 16.9) * mm, "end": v(0, 16.9) * mm});
            skLineSegment(sketch, "E89.left", {"start": v(40, 17.1) * mm, "end": v(40, 16.9) * mm});
            skLineSegment(sketch, "E89.right", {"start": v(0, 17.1) * mm, "end": v(0, 16.9) * mm});
            skLineSegment(sketch, "E90.bottom", {"start": v(40, 16.1) * mm, "end": v(0, 16.1) * mm});
            skLineSegment(sketch, "E90.top", {"start": v(40, 15.9) * mm, "end": v(0, 15.9) * mm});
            skLineSegment(sketch, "E90.left", {"start": v(40, 16.1) * mm, "end": v(40, 15.9) * mm});
            skLineSegment(sketch, "E90.right", {"start": v(0, 16.1) * mm, "end": v(0, 15.9) * mm});
            skLineSegment(sketch, "E91.bottom", {"start": v(40, 15.1) * mm, "end": v(0, 15.1) * mm});
            skLineSegment(sketch, "E91.top", {"start": v(40, 14.9) * mm, "end": v(0, 14.9) * mm});
            skLineSegment(sketch, "E91.left", {"start": v(40, 15.1) * mm, "end": v(40, 14.9) * mm});
            skLineSegment(sketch, "E91.right", {"start": v(0, 15.1) * mm, "end": v(0, 14.9) * mm});
            skLineSegment(sketch, "E92.bottom", {"start": v(40, 14.1) * mm, "end": v(0, 14.1) * mm});
            skLineSegment(sketch, "E92.top", {"start": v(40, 13.9) * mm, "end": v(0, 13.9) * mm});
            skLineSegment(sketch, "E92.left", {"start": v(40, 14.1) * mm, "end": v(40, 13.9) * mm});
            skLineSegment(sketch, "E92.right", {"start": v(0, 14.1) * mm, "end": v(0, 13.9) * mm});
            skLineSegment(sketch, "E93.bottom", {"start": v(40, 13.1) * mm, "end": v(0, 13.1) * mm});
            skLineSegment(sketch, "E93.top", {"start": v(40, 12.9) * mm, "end": v(0, 12.9) * mm});
            skLineSegment(sketch, "E93.left", {"start": v(40, 13.1) * mm, "end": v(40, 12.9) * mm});
            skLineSegment(sketch, "E93.right", {"start": v(0, 13.1) * mm, "end": v(0, 12.9) * mm});
            skLineSegment(sketch, "E94.bottom", {"start": v(40, 12.1) * mm, "end": v(0, 12.1) * mm});
            skLineSegment(sketch, "E94.top", {"start": v(40, 11.9) * mm, "end": v(0, 11.9) * mm});
            skLineSegment(sketch, "E94.left", {"start": v(40, 12.1) * mm, "end": v(40, 11.9) * mm});
            skLineSegment(sketch, "E94.right", {"start": v(0, 12.1) * mm, "end": v(0, 11.9) * mm});
            skLineSegment(sketch, "E95.bottom", {"start": v(40, 11.1) * mm, "end": v(0, 11.1) * mm});
            skLineSegment(sketch, "E95.top", {"start": v(40, 10.9) * mm, "end": v(0, 10.9) * mm});
            skLineSegment(sketch, "E95.left", {"start": v(40, 11.1) * mm, "end": v(40, 10.9) * mm});
            skLineSegment(sketch, "E95.right", {"start": v(0, 11.1) * mm, "end": v(0, 10.9) * mm});
            skLineSegment(sketch, "E96.bottom", {"start": v(40, 10.1) * mm, "end": v(0, 10.1) * mm});
            skLineSegment(sketch, "E96.top", {"start": v(40, 9.9) * mm, "end": v(0, 9.9) * mm});
            skLineSegment(sketch, "E96.left", {"start": v(40, 10.1) * mm, "end": v(40, 9.9) * mm});
            skLineSegment(sketch, "E96.right", {"start": v(0, 10.1) * mm, "end": v(0, 9.9) * mm});
            skLineSegment(sketch, "E97.bottom", {"start": v(40, 9.1) * mm, "end": v(0, 9.1) * mm});
            skLineSegment(sketch, "E97.top", {"start": v(40, 8.9) * mm, "end": v(0, 8.9) * mm});
            skLineSegment(sketch, "E97.left", {"start": v(40, 9.1) * mm, "end": v(40, 8.9) * mm});
            skLineSegment(sketch, "E97.right", {"start": v(0, 9.1) * mm, "end": v(0, 8.9) * mm});
            skLineSegment(sketch, "E98.bottom", {"start": v(40, 8.1) * mm, "end": v(0, 8.1) * mm});
            skLineSegment(sketch, "E98.top", {"start": v(40, 7.9) * mm, "end": v(0, 7.9) * mm});
            skLineSegment(sketch, "E98.left", {"start": v(40, 8.1) * mm, "end": v(40, 7.9) * mm});
            skLineSegment(sketch, "E98.right", {"start": v(0, 8.1) * mm, "end": v(0, 7.9) * mm});
            skLineSegment(sketch, "E99.bottom", {"start": v(40, 7.1) * mm, "end": v(0, 7.1) * mm});
            skLineSegment(sketch, "E99.top", {"start": v(40, 6.9) * mm, "end": v(0, 6.9) * mm});
            skLineSegment(sketch, "E99.left", {"start": v(40, 7.1) * mm, "end": v(40, 6.9) * mm});
            skLineSegment(sketch, "E99.right", {"start": v(0, 7.1) * mm, "end": v(0, 6.9) * mm});
            skLineSegment(sketch, "E100.bottom", {"start": v(40, 6.1) * mm, "end": v(0, 6.1) * mm});
            skLineSegment(sketch, "E100.top", {"start": v(40, 5.9) * mm, "end": v(0, 5.9) * mm});
            skLineSegment(sketch, "E100.left", {"start": v(40, 6.1) * mm, "end": v(40, 5.9) * mm});
            skLineSegment(sketch, "E100.right", {"start": v(0, 6.1) * mm, "end": v(0, 5.9) * mm});
            skLineSegment(sketch, "E101.bottom", {"start": v(40, 5.1) * mm, "end": v(0, 5.1) * mm});
            skLineSegment(sketch, "E101.top", {"start": v(40, 4.9) * mm, "end": v(0, 4.9) * mm});
            skLineSegment(sketch, "E101.left", {"start": v(40, 5.1) * mm, "end": v(40, 4.9) * mm});
            skLineSegment(sketch, "E101.right", {"start": v(0, 5.1) * mm, "end": v(0, 4.9) * mm});
            skLineSegment(sketch, "E102.bottom", {"start": v(40, 4.1) * mm, "end": v(0, 4.1) * mm});
            skLineSegment(sketch, "E102.top", {"start": v(40, 3.9) * mm, "end": v(0, 3.9) * mm});
            skLineSegment(sketch, "E102.left", {"start": v(40, 4.1) * mm, "end": v(40, 3.9) * mm});
            skLineSegment(sketch, "E102.right", {"start": v(0, 4.1) * mm, "end": v(0, 3.9) * mm});
            skLineSegment(sketch, "E103.bottom", {"start": v(40, 2.9) * mm, "end": v(0, 2.9) * mm});
            skLineSegment(sketch, "E103.top", {"start": v(40, 3.1) * mm, "end": v(0, 3.1) * mm});
            skLineSegment(sketch, "E103.left", {"start": v(40, 2.9) * mm, "end": v(40, 3.1) * mm});
            skLineSegment(sketch, "E103.right", {"start": v(0, 2.9) * mm, "end": v(0, 3.1) * mm});
            skLineSegment(sketch, "E104.bottom", {"start": v(40, 1.9) * mm, "end": v(0, 1.9) * mm});
            skLineSegment(sketch, "E104.top", {"start": v(40, 2.1) * mm, "end": v(0, 2.1) * mm});
            skLineSegment(sketch, "E104.left", {"start": v(40, 1.9) * mm, "end": v(40, 2.1) * mm});
            skLineSegment(sketch, "E104.right", {"start": v(0, 1.9) * mm, "end": v(0, 2.1) * mm});
            skLineSegment(sketch, "E105.bottom", {"start": v(40, 0.9) * mm, "end": v(0, 0.9) * mm});
            skLineSegment(sketch, "E105.top", {"start": v(40, 1.1) * mm, "end": v(0, 1.1) * mm});
            skLineSegment(sketch, "E105.left", {"start": v(40, 0.9) * mm, "end": v(40, 1.1) * mm});
            skLineSegment(sketch, "E105.right", {"start": v(0, 0.9) * mm, "end": v(0, 1.1) * mm});
            skSolve(sketch);
        }
        {
            var Q0;
            Q0 = qSketchRegion(id + "F6", true);
            extrude(context, id + "F8", {"entities" : qUnion([Q0]), "operationType" : NewBodyOperationType.REMOVE, "depth" : 1 * mm});
        }
        {
            var Q0;
            Q0 = qSketchRegion(id + "F7", true);
            extrude(context, id + "F9", {"entities" : qUnion([Q0]), "operationType" : NewBodyOperationType.REMOVE, "depth" : 1 * mm});
        }
        {
            var Q0;
            Q0=makeQuery(id+"F1.opExtrude","CAP_FACE",FACE,{"disambiguationData":[OSD([sQuery(id+"F0.wireOp",EDGE,"E0.bottom"),sQuery(id+"F0.wireOp",EDGE,"E0.top"),sQuery(id+"F0.wireOp",EDGE,"E0.left"),sQuery(id+"F0.wireOp",EDGE,"E0.right")])],"isStart":false});
            var sketch = newSketch(context, id + "F10", { "sketchPlane" : qUnion([Q0])});
            skCircle(sketch, "E106", {"center": v(35, -36) * mm, "radius": 1 * mm});
            skCircle(sketch, "E107", {"center": v(35, -4) * mm, "radius": 1 * mm});
            skLineSegment(sketch, "E108.bottom", {"start": v(35, -37) * mm, "end": v(5.1, -37) * mm});
            skLineSegment(sketch, "E108.top", {"start": v(35, -3) * mm, "end": v(5.1, -3) * mm});
            skLineSegment(sketch, "E108.left", {"start": v(35, -37) * mm, "end": v(35, -3) * mm});
            skLineSegment(sketch, "E108.right", {"start": v(5.1, -37) * mm, "end": v(5.1, -3) * mm});
            skLineSegment(sketch, "E109.bottom", {"start": v(4.1, -36) * mm, "end": v(5.1, -36) * mm});
            skLineSegment(sketch, "E109.top", {"start": v(4.1, -4) * mm, "end": v(5.1, -4) * mm});
            skLineSegment(sketch, "E109.left", {"start": v(4.1, -36) * mm, "end": v(4.1, -4) * mm});
            skLineSegment(sketch, "E109.right", {"start": v(5.1, -36) * mm, "end": v(5.1, -4) * mm});
            skLineSegment(sketch, "E110.bottom", {"start": v(36, -36) * mm, "end": v(35, -36) * mm});
            skLineSegment(sketch, "E110.top", {"start": v(36, -4) * mm, "end": v(35, -4) * mm});
            skLineSegment(sketch, "E110.left", {"start": v(36, -36) * mm, "end": v(36, -4) * mm});
            skLineSegment(sketch, "E110.right", {"start": v(35, -36) * mm, "end": v(35, -4) * mm});
            skLineSegment(sketch, "E111.bottom", {"start": v(36, -29) * mm, "end": v(37, -29) * mm});
            skLineSegment(sketch, "E111.top", {"start": v(36, -11) * mm, "end": v(37, -11) * mm});
            skLineSegment(sketch, "E111.left", {"start": v(36, -29) * mm, "end": v(36, -11) * mm});
            skLineSegment(sketch, "E111.right", {"start": v(37, -29) * mm, "end": v(37, -11) * mm});
            skLineSegment(sketch, "E112.bottom", {"start": v(4.1, -29) * mm, "end": v(3.1, -29) * mm});
            skLineSegment(sketch, "E112.top", {"start": v(4.1, -11) * mm, "end": v(3.1, -11) * mm});
            skLineSegment(sketch, "E112.left", {"start": v(4.1, -29) * mm, "end": v(4.1, -11) * mm});
            skLineSegment(sketch, "E112.right", {"start": v(3.1, -29) * mm, "end": v(3.1, -11) * mm});
            skLineSegment(sketch, "E113.bottom", {"start": v(3.1, -27) * mm, "end": v(2.1, -27) * mm});
            skLineSegment(sketch, "E113.top", {"start": v(3.1, -13) * mm, "end": v(2.1, -13) * mm});
            skLineSegment(sketch, "E113.left", {"start": v(3.1, -27) * mm, "end": v(3.1, -13) * mm});
            skLineSegment(sketch, "E113.right", {"start": v(2.1, -27) * mm, "end": v(2.1, -13) * mm});
            skLineSegment(sketch, "E114.bottom", {"start": v(37, -27) * mm, "end": v(38, -27) * mm});
            skLineSegment(sketch, "E114.top", {"start": v(37, -13) * mm, "end": v(38, -13) * mm});
            skLineSegment(sketch, "E114.left", {"start": v(37, -27) * mm, "end": v(37, -13) * mm});
            skLineSegment(sketch, "E114.right", {"start": v(38, -27) * mm, "end": v(38, -13) * mm});
            skCircle(sketch, "E115", {"center": v(5.1, -36) * mm, "radius": 1 * mm});
            skCircle(sketch, "E116", {"center": v(5.1, -4) * mm, "radius": 1 * mm});
            skSolve(sketch);
        }
        {
            var Q0;
            Q0 = qSketchRegion(id + "F10", true);
            extrude(context, id + "F11", {"entities" : qUnion([Q0]), "depth" : 1 * mm});
        }
        {
            var Q0;
            Q0=makeQuery(id+"F11.opExtrude","CAP_FACE",FACE,{"disambiguationData":[OSD([sQuery(id+"F10.wireOp",EDGE,"E106"),sQuery(id+"F10.wireOp",EDGE,"E107"),sQuery(id+"F10.wireOp",EDGE,"BgA77Dz9-5KGh-Efrp-Hv6M-BgwUDxvD4Rni"),sQuery(id+"F10.wireOp",EDGE,"gzdvfRr6-IRiG-GsUh-SExL-255vmCyJLMX6"),sQuery(id+"F10.wireOp",EDGE,"E108.bottom"),sQuery(id+"F10.wireOp",EDGE,"E108.top"),sQuery(id+"F10.wireOp",EDGE,"E108.right"),sQuery(id+"F10.wireOp",EDGE,"E109.left"),sQuery(id+"F10.wireOp",EDGE,"E110.left"),sQuery(id+"F10.wireOp",EDGE,"E111.bottom"),sQuery(id+"F10.wireOp",EDGE,"E111.top"),sQuery(id+"F10.wireOp",EDGE,"E111.right"),sQuery(id+"F10.wireOp",EDGE,"E112.bottom"),sQuery(id+"F10.wireOp",EDGE,"E112.top"),sQuery(id+"F10.wireOp",EDGE,"E112.right"),sQuery(id+"F10.wireOp",EDGE,"E113.bottom"),sQuery(id+"F10.wireOp",EDGE,"E113.top"),sQuery(id+"F10.wireOp",EDGE,"E113.right"),sQuery(id+"F10.wireOp",EDGE,"E114.bottom"),sQuery(id+"F10.wireOp",EDGE,"E114.top"),sQuery(id+"F10.wireOp",EDGE,"E114.right")])],"isStart":false});
            var sketch = newSketch(context, id + "F12", { "sketchPlane" : qUnion([Q0])});
            skCircle(sketch, "E117", {"center": v(37, -27) * mm, "radius": 1 * mm});
            skCircle(sketch, "E118", {"center": v(37, -13) * mm, "radius": 1 * mm});
            skCircle(sketch, "E119", {"center": v(3.1, -13) * mm, "radius": 1 * mm});
            skCircle(sketch, "E120", {"center": v(3.1, -27) * mm, "radius": 1 * mm});
            skSolve(sketch);
        }
        {
            var Q0;
            Q0 = qSketchRegion(id + "F12", true);
            extrude(context, id + "F13", {"entities" : qUnion([Q0]), "operationType" : NewBodyOperationType.ADD, "oppositeDirection" : true, "depth" : 1 * mm});
        }
        {
            var Q0;
            Q0=makeQuery(id+"F13.boolean.opBoolean","MERGE",FACE,{"derivedFrom":[makeQuery(id+"F11.opExtrude","CAP_FACE",FACE,{"disambiguationData":[OSD([sQuery(id+"F10.wireOp",EDGE,"E106"),sQuery(id+"F10.wireOp",EDGE,"E107"),sQuery(id+"F10.wireOp",EDGE,"BgA77Dz9-5KGh-Efrp-Hv6M-BgwUDxvD4Rni"),sQuery(id+"F10.wireOp",EDGE,"gzdvfRr6-IRiG-GsUh-SExL-255vmCyJLMX6"),sQuery(id+"F10.wireOp",EDGE,"E108.bottom"),sQuery(id+"F10.wireOp",EDGE,"E108.top"),sQuery(id+"F10.wireOp",EDGE,"E108.right"),sQuery(id+"F10.wireOp",EDGE,"E109.left"),sQuery(id+"F10.wireOp",EDGE,"E110.left"),sQuery(id+"F10.wireOp",EDGE,"E111.bottom"),sQuery(id+"F10.wireOp",EDGE,"E111.top"),sQuery(id+"F10.wireOp",EDGE,"E111.right"),sQuery(id+"F10.wireOp",EDGE,"E112.bottom"),sQuery(id+"F10.wireOp",EDGE,"E112.top"),sQuery(id+"F10.wireOp",EDGE,"E112.right"),sQuery(id+"F10.wireOp",EDGE,"E113.bottom"),sQuery(id+"F10.wireOp",EDGE,"E113.top"),sQuery(id+"F10.wireOp",EDGE,"E113.right"),sQuery(id+"F10.wireOp",EDGE,"E114.bottom"),sQuery(id+"F10.wireOp",EDGE,"E114.top"),sQuery(id+"F10.wireOp",EDGE,"E114.right")])],"isStart":false}),makeQuery(id+"F13.opExtrude","CAP_FACE",FACE,{"disambiguationData":[OSD([sQuery(id+"F12.wireOp",EDGE,"E117")])],"isStart":true}),makeQuery(id+"F13.opExtrude","CAP_FACE",FACE,{"disambiguationData":[OSD([sQuery(id+"F12.wireOp",EDGE,"E118")])],"isStart":true}),makeQuery(id+"F13.opExtrude","CAP_FACE",FACE,{"disambiguationData":[OSD([sQuery(id+"F12.wireOp",EDGE,"E119")])],"isStart":true}),makeQuery(id+"F13.opExtrude","CAP_FACE",FACE,{"disambiguationData":[OSD([sQuery(id+"F12.wireOp",EDGE,"E120")])],"isStart":true})]});
            var sketch = newSketch(context, id + "F14", { "sketchPlane" : qUnion([Q0])});
            skCircle(sketch, "E121", {"center": v(37, -29) * mm, "radius": 1 * mm});
            skCircle(sketch, "E122", {"center": v(37, -11) * mm, "radius": 1 * mm});
            skCircle(sketch, "E123", {"center": v(3.1, -29) * mm, "radius": 1 * mm});
            skCircle(sketch, "E124", {"center": v(3.1, -11) * mm, "radius": 1 * mm});
            skSolve(sketch);
        }
        {
            var Q0;
            Q0 = qSketchRegion(id + "F14", true);
            extrude(context, id + "F15", {"entities" : qUnion([Q0]), "operationType" : NewBodyOperationType.REMOVE, "oppositeDirection" : true, "depth" : 1 * mm});
        }
        {
            var Q0;
            Q0=makeQuery(id+"F13.boolean.opBoolean","MERGE",FACE,{"derivedFrom":[makeQuery(id+"F11.opExtrude","CAP_FACE",FACE,{"disambiguationData":[OSD([sQuery(id+"F10.wireOp",EDGE,"E106"),sQuery(id+"F10.wireOp",EDGE,"E107"),sQuery(id+"F10.wireOp",EDGE,"E108.bottom"),sQuery(id+"F10.wireOp",EDGE,"E108.top"),sQuery(id+"F10.wireOp",EDGE,"E109.left"),sQuery(id+"F10.wireOp",EDGE,"E110.left"),sQuery(id+"F10.wireOp",EDGE,"E111.bottom"),sQuery(id+"F10.wireOp",EDGE,"E111.top"),sQuery(id+"F10.wireOp",EDGE,"E111.right"),sQuery(id+"F10.wireOp",EDGE,"E112.bottom"),sQuery(id+"F10.wireOp",EDGE,"E112.top"),sQuery(id+"F10.wireOp",EDGE,"E112.right"),sQuery(id+"F10.wireOp",EDGE,"E113.bottom"),sQuery(id+"F10.wireOp",EDGE,"E113.top"),sQuery(id+"F10.wireOp",EDGE,"E113.right"),sQuery(id+"F10.wireOp",EDGE,"E114.bottom"),sQuery(id+"F10.wireOp",EDGE,"E114.top"),sQuery(id+"F10.wireOp",EDGE,"E114.right"),sQuery(id+"F10.wireOp",EDGE,"E115"),sQuery(id+"F10.wireOp",EDGE,"E116")])],"isStart":false}),makeQuery(id+"F13.opExtrude","CAP_FACE",FACE,{"disambiguationData":[OSD([sQuery(id+"F12.wireOp",EDGE,"E117")])],"isStart":true}),makeQuery(id+"F13.opExtrude","CAP_FACE",FACE,{"disambiguationData":[OSD([sQuery(id+"F12.wireOp",EDGE,"E118")])],"isStart":true}),makeQuery(id+"F13.opExtrude","CAP_FACE",FACE,{"disambiguationData":[OSD([sQuery(id+"F12.wireOp",EDGE,"E119")])],"isStart":true}),makeQuery(id+"F13.opExtrude","CAP_FACE",FACE,{"disambiguationData":[OSD([sQuery(id+"F12.wireOp",EDGE,"E120")])],"isStart":true})]});
            var sketch = newSketch(context, id + "F16", { "sketchPlane" : qUnion([Q0])});
            skLineSegment(sketch, "E125.bottom", {"start": v(34, -36) * mm, "end": v(6.1, -36) * mm});
            skLineSegment(sketch, "E125.top", {"start": v(34, -4) * mm, "end": v(6.1, -4) * mm});
            skLineSegment(sketch, "E125.left", {"start": v(34, -36) * mm, "end": v(34, -4) * mm});
            skLineSegment(sketch, "E125.right", {"start": v(6.1, -36) * mm, "end": v(6.1, -4) * mm});
            skLineSegment(sketch, "E126.bottom", {"start": v(34, -35) * mm, "end": v(35, -35) * mm});
            skLineSegment(sketch, "E126.top", {"start": v(34, -5) * mm, "end": v(35, -5) * mm});
            skLineSegment(sketch, "E126.left", {"start": v(34, -35) * mm, "end": v(34, -5) * mm});
            skLineSegment(sketch, "E126.right", {"start": v(35, -35) * mm, "end": v(35, -5) * mm});
            skLineSegment(sketch, "E127.bottom", {"start": v(6.1, -35) * mm, "end": v(5.1, -35) * mm});
            skLineSegment(sketch, "E127.top", {"start": v(6.1, -5) * mm, "end": v(5.1, -5) * mm});
            skLineSegment(sketch, "E127.left", {"start": v(6.1, -35) * mm, "end": v(6.1, -5) * mm});
            skLineSegment(sketch, "E127.right", {"start": v(5.1, -35) * mm, "end": v(5.1, -5) * mm});
            skCircle(sketch, "E128", {"center": v(34, -35) * mm, "radius": 1 * mm});
            skCircle(sketch, "E129", {"center": v(6.1, -35) * mm, "radius": 1 * mm});
            skCircle(sketch, "E130", {"center": v(6.1, -5) * mm, "radius": 1 * mm});
            skCircle(sketch, "E131", {"center": v(34, -5) * mm, "radius": 1 * mm});
            skSolve(sketch);
        }
        {
            var Q0;
            Q0 = qSketchRegion(id + "F16", true);
            extrude(context, id + "F17", {"entities" : qUnion([Q0]), "operationType" : NewBodyOperationType.ADD, "depth" : 2 * mm});
        }
        {
            var Q0;
            Q0=makeQuery(id+"F1.opExtrude","CAP_FACE",FACE,{"disambiguationData":[OSD([sQuery(id+"F0.wireOp",EDGE,"E0.bottom"),sQuery(id+"F0.wireOp",EDGE,"E0.top"),sQuery(id+"F0.wireOp",EDGE,"E0.left"),sQuery(id+"F0.wireOp",EDGE,"E0.right")])],"isStart":true});
            var sketch = newSketch(context, id + "F18", { "sketchPlane" : qUnion([Q0])});
            skLineSegment(sketch, "E132.bottom", {"start": v(19.1, 27.7) * mm, "end": v(19.9, 27.7) * mm});
            skLineSegment(sketch, "E132.top", {"start": v(19.1, 27.3) * mm, "end": v(19.9, 27.3) * mm});
            skLineSegment(sketch, "E132.left", {"start": v(19.1, 27.7) * mm, "end": v(19.1, 27.3) * mm});
            skLineSegment(sketch, "E132.right", {"start": v(19.9, 27.7) * mm, "end": v(19.9, 27.3) * mm});
            skLineSegment(sketch, "E133.bottom", {"start": v(19.1, 26.7) * mm, "end": v(19.9, 26.7) * mm});
            skLineSegment(sketch, "E133.top", {"start": v(19.1, 26.3) * mm, "end": v(19.9, 26.3) * mm});
            skLineSegment(sketch, "E133.left", {"start": v(19.1, 26.7) * mm, "end": v(19.1, 26.3) * mm});
            skLineSegment(sketch, "E133.right", {"start": v(19.9, 26.7) * mm, "end": v(19.9, 26.3) * mm});
            skLineSegment(sketch, "E134.bottom", {"start": v(19.1, 25.7) * mm, "end": v(19.9, 25.7) * mm});
            skLineSegment(sketch, "E134.top", {"start": v(19.1, 25.3) * mm, "end": v(19.9, 25.3) * mm});
            skLineSegment(sketch, "E134.left", {"start": v(19.1, 25.7) * mm, "end": v(19.1, 25.3) * mm});
            skLineSegment(sketch, "E134.right", {"start": v(19.9, 25.7) * mm, "end": v(19.9, 25.3) * mm});
            skLineSegment(sketch, "E135.bottom", {"start": v(19.1, 24.7) * mm, "end": v(19.9, 24.7) * mm});
            skLineSegment(sketch, "E135.top", {"start": v(19.1, 24.3) * mm, "end": v(19.9, 24.3) * mm});
            skLineSegment(sketch, "E135.left", {"start": v(19.1, 24.7) * mm, "end": v(19.1, 24.3) * mm});
            skLineSegment(sketch, "E135.right", {"start": v(19.9, 24.7) * mm, "end": v(19.9, 24.3) * mm});
            skLineSegment(sketch, "E136.bottom", {"start": v(19.1, 23.7) * mm, "end": v(19.9, 23.7) * mm});
            skLineSegment(sketch, "E136.top", {"start": v(19.1, 23.3) * mm, "end": v(19.9, 23.3) * mm});
            skLineSegment(sketch, "E136.left", {"start": v(19.1, 23.7) * mm, "end": v(19.1, 23.3) * mm});
            skLineSegment(sketch, "E136.right", {"start": v(19.9, 23.7) * mm, "end": v(19.9, 23.3) * mm});
            skLineSegment(sketch, "E137.bottom", {"start": v(19.1, 22.7) * mm, "end": v(19.9, 22.7) * mm});
            skLineSegment(sketch, "E137.top", {"start": v(19.1, 22.3) * mm, "end": v(19.9, 22.3) * mm});
            skLineSegment(sketch, "E137.left", {"start": v(19.1, 22.7) * mm, "end": v(19.1, 22.3) * mm});
            skLineSegment(sketch, "E137.right", {"start": v(19.9, 22.7) * mm, "end": v(19.9, 22.3) * mm});
            skLineSegment(sketch, "E138.bottom", {"start": v(19.1, 21.7) * mm, "end": v(19.9, 21.7) * mm});
            skLineSegment(sketch, "E138.top", {"start": v(19.1, 21.3) * mm, "end": v(19.9, 21.3) * mm});
            skLineSegment(sketch, "E138.left", {"start": v(19.1, 21.7) * mm, "end": v(19.1, 21.3) * mm});
            skLineSegment(sketch, "E138.right", {"start": v(19.9, 21.7) * mm, "end": v(19.9, 21.3) * mm});
            skLineSegment(sketch, "E139.bottom", {"start": v(14.9, 21.3) * mm, "end": v(15.7, 21.3) * mm});
            skLineSegment(sketch, "E139.top", {"start": v(14.9, 21.7) * mm, "end": v(15.7, 21.7) * mm});
            skLineSegment(sketch, "E139.left", {"start": v(14.9, 21.3) * mm, "end": v(14.9, 21.7) * mm});
            skLineSegment(sketch, "E139.right", {"start": v(15.7, 21.3) * mm, "end": v(15.7, 21.7) * mm});
            skLineSegment(sketch, "E140.bottom", {"start": v(14.9, 22.3) * mm, "end": v(15.7, 22.3) * mm});
            skLineSegment(sketch, "E140.top", {"start": v(14.9, 22.7) * mm, "end": v(15.7, 22.7) * mm});
            skLineSegment(sketch, "E140.left", {"start": v(14.9, 22.3) * mm, "end": v(14.9, 22.7) * mm});
            skLineSegment(sketch, "E140.right", {"start": v(15.7, 22.3) * mm, "end": v(15.7, 22.7) * mm});
            skLineSegment(sketch, "E141.bottom", {"start": v(14.9, 23.3) * mm, "end": v(15.7, 23.3) * mm});
            skLineSegment(sketch, "E141.top", {"start": v(14.9, 23.7) * mm, "end": v(15.7, 23.7) * mm});
            skLineSegment(sketch, "E141.left", {"start": v(14.9, 23.3) * mm, "end": v(14.9, 23.7) * mm});
            skLineSegment(sketch, "E141.right", {"start": v(15.7, 23.3) * mm, "end": v(15.7, 23.7) * mm});
            skLineSegment(sketch, "E142.bottom", {"start": v(15.7, 24.3) * mm, "end": v(14.9, 24.3) * mm});
            skLineSegment(sketch, "E142.top", {"start": v(15.7, 24.7) * mm, "end": v(14.9, 24.7) * mm});
            skLineSegment(sketch, "E142.left", {"start": v(15.7, 24.3) * mm, "end": v(15.7, 24.7) * mm});
            skLineSegment(sketch, "E142.right", {"start": v(14.9, 24.3) * mm, "end": v(14.9, 24.7) * mm});
            skLineSegment(sketch, "E143.bottom", {"start": v(15.7, 25.3) * mm, "end": v(14.9, 25.3) * mm});
            skLineSegment(sketch, "E143.top", {"start": v(15.7, 25.7) * mm, "end": v(14.9, 25.7) * mm});
            skLineSegment(sketch, "E143.left", {"start": v(15.7, 25.3) * mm, "end": v(15.7, 25.7) * mm});
            skLineSegment(sketch, "E143.right", {"start": v(14.9, 25.3) * mm, "end": v(14.9, 25.7) * mm});
            skLineSegment(sketch, "E144.bottom", {"start": v(18.9, 20.7) * mm, "end": v(18.1, 20.7) * mm});
            skLineSegment(sketch, "E144.top", {"start": v(18.9, 20.3) * mm, "end": v(18.1, 20.3) * mm});
            skLineSegment(sketch, "E144.left", {"start": v(18.9, 20.7) * mm, "end": v(18.9, 20.3) * mm});
            skLineSegment(sketch, "E144.right", {"start": v(18.1, 20.7) * mm, "end": v(18.1, 20.3) * mm});
            skLineSegment(sketch, "E145.bottom", {"start": v(18.9, 19.7) * mm, "end": v(18.1, 19.7) * mm});
            skLineSegment(sketch, "E145.top", {"start": v(18.9, 19.3) * mm, "end": v(18.1, 19.3) * mm});
            skLineSegment(sketch, "E145.left", {"start": v(18.9, 19.7) * mm, "end": v(18.9, 19.3) * mm});
            skLineSegment(sketch, "E145.right", {"start": v(18.1, 19.7) * mm, "end": v(18.1, 19.3) * mm});
            skLineSegment(sketch, "E146.bottom", {"start": v(18.9, 18.7) * mm, "end": v(18.1, 18.7) * mm});
            skLineSegment(sketch, "E146.top", {"start": v(18.9, 18.3) * mm, "end": v(18.1, 18.3) * mm});
            skLineSegment(sketch, "E146.left", {"start": v(18.9, 18.7) * mm, "end": v(18.9, 18.3) * mm});
            skLineSegment(sketch, "E146.right", {"start": v(18.1, 18.7) * mm, "end": v(18.1, 18.3) * mm});
            skLineSegment(sketch, "E147.bottom", {"start": v(15.9, 20.9) * mm, "end": v(16.3, 20.9) * mm});
            skLineSegment(sketch, "E147.top", {"start": v(15.9, 20.1) * mm, "end": v(16.3, 20.1) * mm});
            skLineSegment(sketch, "E147.left", {"start": v(15.9, 20.9) * mm, "end": v(15.9, 20.1) * mm});
            skLineSegment(sketch, "E147.right", {"start": v(16.3, 20.9) * mm, "end": v(16.3, 20.1) * mm});
            skLineSegment(sketch, "E148.bottom", {"start": v(16.9, 20.9) * mm, "end": v(17.3, 20.9) * mm});
            skLineSegment(sketch, "E148.top", {"start": v(16.9, 20.1) * mm, "end": v(17.3, 20.1) * mm});
            skLineSegment(sketch, "E148.left", {"start": v(16.9, 20.9) * mm, "end": v(16.9, 20.1) * mm});
            skLineSegment(sketch, "E148.right", {"start": v(17.3, 20.9) * mm, "end": v(17.3, 20.1) * mm});
            skLineSegment(sketch, "E149.bottom", {"start": v(16.9, 19.7) * mm, "end": v(16.1, 19.7) * mm});
            skLineSegment(sketch, "E149.top", {"start": v(16.9, 19.3) * mm, "end": v(16.1, 19.3) * mm});
            skLineSegment(sketch, "E149.left", {"start": v(16.9, 19.7) * mm, "end": v(16.9, 19.3) * mm});
            skLineSegment(sketch, "E149.right", {"start": v(16.1, 19.7) * mm, "end": v(16.1, 19.3) * mm});
            skLineSegment(sketch, "E150.bottom", {"start": v(16.9, 18.7) * mm, "end": v(16.1, 18.7) * mm});
            skLineSegment(sketch, "E150.top", {"start": v(16.9, 18.3) * mm, "end": v(16.1, 18.3) * mm});
            skLineSegment(sketch, "E150.left", {"start": v(16.9, 18.7) * mm, "end": v(16.9, 18.3) * mm});
            skLineSegment(sketch, "E150.right", {"start": v(16.1, 18.7) * mm, "end": v(16.1, 18.3) * mm});
            skLineSegment(sketch, "E151.bottom", {"start": v(16.9, 17.7) * mm, "end": v(16.1, 17.7) * mm});
            skLineSegment(sketch, "E151.top", {"start": v(16.9, 17.3) * mm, "end": v(16.1, 17.3) * mm});
            skLineSegment(sketch, "E151.left", {"start": v(16.9, 17.7) * mm, "end": v(16.9, 17.3) * mm});
            skLineSegment(sketch, "E151.right", {"start": v(16.1, 17.7) * mm, "end": v(16.1, 17.3) * mm});
            skLineSegment(sketch, "E152.bottom", {"start": v(16.9, 16.7) * mm, "end": v(16.1, 16.7) * mm});
            skLineSegment(sketch, "E152.top", {"start": v(16.9, 16.3) * mm, "end": v(16.1, 16.3) * mm});
            skLineSegment(sketch, "E152.left", {"start": v(16.9, 16.7) * mm, "end": v(16.9, 16.3) * mm});
            skLineSegment(sketch, "E152.right", {"start": v(16.1, 16.7) * mm, "end": v(16.1, 16.3) * mm});
            skLineSegment(sketch, "E153.bottom", {"start": v(16.1, 15.7) * mm, "end": v(16.9, 15.7) * mm});
            skLineSegment(sketch, "E153.top", {"start": v(16.1, 15.3) * mm, "end": v(16.9, 15.3) * mm});
            skLineSegment(sketch, "E153.left", {"start": v(16.1, 15.7) * mm, "end": v(16.1, 15.3) * mm});
            skLineSegment(sketch, "E153.right", {"start": v(16.9, 15.7) * mm, "end": v(16.9, 15.3) * mm});
            skLineSegment(sketch, "E154.bottom", {"start": v(16.9, 14.7) * mm, "end": v(16.1, 14.7) * mm});
            skLineSegment(sketch, "E154.top", {"start": v(16.9, 14.3) * mm, "end": v(16.1, 14.3) * mm});
            skLineSegment(sketch, "E154.left", {"start": v(16.9, 14.7) * mm, "end": v(16.9, 14.3) * mm});
            skLineSegment(sketch, "E154.right", {"start": v(16.1, 14.7) * mm, "end": v(16.1, 14.3) * mm});
            skLineSegment(sketch, "E155.bottom", {"start": v(16.1, 13.7) * mm, "end": v(16.9, 13.7) * mm});
            skLineSegment(sketch, "E155.top", {"start": v(16.1, 13.3) * mm, "end": v(16.9, 13.3) * mm});
            skLineSegment(sketch, "E155.left", {"start": v(16.1, 13.7) * mm, "end": v(16.1, 13.3) * mm});
            skLineSegment(sketch, "E155.right", {"start": v(16.9, 13.7) * mm, "end": v(16.9, 13.3) * mm});
            skLineSegment(sketch, "E156.bottom", {"start": v(16.9, 12.7) * mm, "end": v(16.1, 12.7) * mm});
            skLineSegment(sketch, "E156.top", {"start": v(16.9, 12.3) * mm, "end": v(16.1, 12.3) * mm});
            skLineSegment(sketch, "E156.left", {"start": v(16.9, 12.7) * mm, "end": v(16.9, 12.3) * mm});
            skLineSegment(sketch, "E156.right", {"start": v(16.1, 12.7) * mm, "end": v(16.1, 12.3) * mm});
            skLineSegment(sketch, "E157.bottom", {"start": v(16.1, 11.7) * mm, "end": v(16.9, 11.7) * mm});
            skLineSegment(sketch, "E157.top", {"start": v(16.1, 11.3) * mm, "end": v(16.9, 11.3) * mm});
            skLineSegment(sketch, "E157.left", {"start": v(16.1, 11.7) * mm, "end": v(16.1, 11.3) * mm});
            skLineSegment(sketch, "E157.right", {"start": v(16.9, 11.7) * mm, "end": v(16.9, 11.3) * mm});
            skLineSegment(sketch, "E158.bottom", {"start": v(16.1, 9.7) * mm, "end": v(16.9, 9.7) * mm});
            skLineSegment(sketch, "E158.top", {"start": v(16.1, 9.3) * mm, "end": v(16.9, 9.3) * mm});
            skLineSegment(sketch, "E158.left", {"start": v(16.1, 9.7) * mm, "end": v(16.1, 9.3) * mm});
            skLineSegment(sketch, "E158.right", {"start": v(16.9, 9.7) * mm, "end": v(16.9, 9.3) * mm});
            skLineSegment(sketch, "E159.bottom", {"start": v(17.3, 9.4) * mm, "end": v(17.7, 9.4) * mm});
            skLineSegment(sketch, "E159.top", {"start": v(17.3, 10.2) * mm, "end": v(17.7, 10.2) * mm});
            skLineSegment(sketch, "E159.left", {"start": v(17.3, 9.4) * mm, "end": v(17.3, 10.2) * mm});
            skLineSegment(sketch, "E159.right", {"start": v(17.7, 9.4) * mm, "end": v(17.7, 10.2) * mm});
            skLineSegment(sketch, "E160.bottom", {"start": v(17.7, 11.8) * mm, "end": v(17.3, 11.8) * mm});
            skLineSegment(sketch, "E160.top", {"start": v(17.7, 11) * mm, "end": v(17.3, 11) * mm});
            skLineSegment(sketch, "E160.left", {"start": v(17.7, 11.8) * mm, "end": v(17.7, 11) * mm});
            skLineSegment(sketch, "E160.right", {"start": v(17.3, 11.8) * mm, "end": v(17.3, 11) * mm});
            skLineSegment(sketch, "E161.bottom", {"start": v(17.7, 13.4) * mm, "end": v(17.3, 13.4) * mm});
            skLineSegment(sketch, "E161.top", {"start": v(17.7, 12.6) * mm, "end": v(17.3, 12.6) * mm});
            skLineSegment(sketch, "E161.left", {"start": v(17.7, 13.4) * mm, "end": v(17.7, 12.6) * mm});
            skLineSegment(sketch, "E161.right", {"start": v(17.3, 13.4) * mm, "end": v(17.3, 12.6) * mm});
            skLineSegment(sketch, "E162.bottom", {"start": v(15.3, 19.4) * mm, "end": v(15.7, 19.4) * mm});
            skLineSegment(sketch, "E162.top", {"start": v(15.3, 18.6) * mm, "end": v(15.7, 18.6) * mm});
            skLineSegment(sketch, "E162.left", {"start": v(15.3, 19.4) * mm, "end": v(15.3, 18.6) * mm});
            skLineSegment(sketch, "E162.right", {"start": v(15.7, 19.4) * mm, "end": v(15.7, 18.6) * mm});
            skLineSegment(sketch, "E163.bottom", {"start": v(15.3, 17.8) * mm, "end": v(15.7, 17.8) * mm});
            skLineSegment(sketch, "E163.top", {"start": v(15.3, 17) * mm, "end": v(15.7, 17) * mm});
            skLineSegment(sketch, "E163.left", {"start": v(15.3, 17.8) * mm, "end": v(15.3, 17) * mm});
            skLineSegment(sketch, "E163.right", {"start": v(15.7, 17.8) * mm, "end": v(15.7, 17) * mm});
            skLineSegment(sketch, "E164.bottom", {"start": v(15.3, 16.2) * mm, "end": v(15.7, 16.2) * mm});
            skLineSegment(sketch, "E164.top", {"start": v(15.3, 15.4) * mm, "end": v(15.7, 15.4) * mm});
            skLineSegment(sketch, "E164.left", {"start": v(15.3, 16.2) * mm, "end": v(15.3, 15.4) * mm});
            skLineSegment(sketch, "E164.right", {"start": v(15.7, 16.2) * mm, "end": v(15.7, 15.4) * mm});
            skLineSegment(sketch, "E165.bottom", {"start": v(15.3, 14.6) * mm, "end": v(15.7, 14.6) * mm});
            skLineSegment(sketch, "E165.top", {"start": v(15.3, 13.8) * mm, "end": v(15.7, 13.8) * mm});
            skLineSegment(sketch, "E165.left", {"start": v(15.3, 14.6) * mm, "end": v(15.3, 13.8) * mm});
            skLineSegment(sketch, "E165.right", {"start": v(15.7, 14.6) * mm, "end": v(15.7, 13.8) * mm});
            skLineSegment(sketch, "E166.bottom", {"start": v(15.3, 13) * mm, "end": v(15.7, 13) * mm});
            skLineSegment(sketch, "E166.top", {"start": v(15.3, 12.2) * mm, "end": v(15.7, 12.2) * mm});
            skLineSegment(sketch, "E166.left", {"start": v(15.3, 13) * mm, "end": v(15.3, 12.2) * mm});
            skLineSegment(sketch, "E166.right", {"start": v(15.7, 13) * mm, "end": v(15.7, 12.2) * mm});
            skLineSegment(sketch, "E167.bottom", {"start": v(15.3, 11.4) * mm, "end": v(15.7, 11.4) * mm});
            skLineSegment(sketch, "E167.top", {"start": v(15.3, 10.6) * mm, "end": v(15.7, 10.6) * mm});
            skLineSegment(sketch, "E167.left", {"start": v(15.3, 11.4) * mm, "end": v(15.3, 10.6) * mm});
            skLineSegment(sketch, "E167.right", {"start": v(15.7, 11.4) * mm, "end": v(15.7, 10.6) * mm});
            skLineSegment(sketch, "E168.bottom", {"start": v(25.7, 9.4) * mm, "end": v(25.3, 9.4) * mm});
            skLineSegment(sketch, "E168.top", {"start": v(25.7, 10.2) * mm, "end": v(25.3, 10.2) * mm});
            skLineSegment(sketch, "E168.left", {"start": v(25.7, 9.4) * mm, "end": v(25.7, 10.2) * mm});
            skLineSegment(sketch, "E168.right", {"start": v(25.3, 9.4) * mm, "end": v(25.3, 10.2) * mm});
            skLineSegment(sketch, "E169.bottom", {"start": v(25.7, 11) * mm, "end": v(25.3, 11) * mm});
            skLineSegment(sketch, "E169.top", {"start": v(25.7, 11.8) * mm, "end": v(25.3, 11.8) * mm});
            skLineSegment(sketch, "E169.left", {"start": v(25.7, 11) * mm, "end": v(25.7, 11.8) * mm});
            skLineSegment(sketch, "E169.right", {"start": v(25.3, 11) * mm, "end": v(25.3, 11.8) * mm});
            skLineSegment(sketch, "E170.bottom", {"start": v(25.7, 12.6) * mm, "end": v(25.3, 12.6) * mm});
            skLineSegment(sketch, "E170.top", {"start": v(25.7, 13.4) * mm, "end": v(25.3, 13.4) * mm});
            skLineSegment(sketch, "E170.left", {"start": v(25.7, 12.6) * mm, "end": v(25.7, 13.4) * mm});
            skLineSegment(sketch, "E170.right", {"start": v(25.3, 12.6) * mm, "end": v(25.3, 13.4) * mm});
            skLineSegment(sketch, "E171.bottom", {"start": v(25.3, 14.2) * mm, "end": v(25.7, 14.2) * mm});
            skLineSegment(sketch, "E171.top", {"start": v(25.3, 15) * mm, "end": v(25.7, 15) * mm});
            skLineSegment(sketch, "E171.left", {"start": v(25.3, 14.2) * mm, "end": v(25.3, 15) * mm});
            skLineSegment(sketch, "E171.right", {"start": v(25.7, 14.2) * mm, "end": v(25.7, 15) * mm});
            skLineSegment(sketch, "E172.bottom", {"start": v(25.3, 15.8) * mm, "end": v(25.7, 15.8) * mm});
            skLineSegment(sketch, "E172.top", {"start": v(25.3, 16.6) * mm, "end": v(25.7, 16.6) * mm});
            skLineSegment(sketch, "E172.left", {"start": v(25.3, 15.8) * mm, "end": v(25.3, 16.6) * mm});
            skLineSegment(sketch, "E172.right", {"start": v(25.7, 15.8) * mm, "end": v(25.7, 16.6) * mm});
            skLineSegment(sketch, "E173.bottom", {"start": v(25.3, 17.4) * mm, "end": v(25.7, 17.4) * mm});
            skLineSegment(sketch, "E173.top", {"start": v(25.3, 18.2) * mm, "end": v(25.7, 18.2) * mm});
            skLineSegment(sketch, "E173.left", {"start": v(25.3, 17.4) * mm, "end": v(25.3, 18.2) * mm});
            skLineSegment(sketch, "E173.right", {"start": v(25.7, 17.4) * mm, "end": v(25.7, 18.2) * mm});
            skLineSegment(sketch, "E174.bottom", {"start": v(25.3, 19) * mm, "end": v(25.7, 19) * mm});
            skLineSegment(sketch, "E174.top", {"start": v(25.3, 19.8) * mm, "end": v(25.7, 19.8) * mm});
            skLineSegment(sketch, "E174.left", {"start": v(25.3, 19) * mm, "end": v(25.3, 19.8) * mm});
            skLineSegment(sketch, "E174.right", {"start": v(25.7, 19) * mm, "end": v(25.7, 19.8) * mm});
            skSolve(sketch);
        }
        {
            var Q0;
            Q0 = qSketchRegion(id + "F18", true);
            extrude(context, id + "F19", {"entities" : qUnion([Q0]), "depth" : 0.2 * mm});
        }
    });
